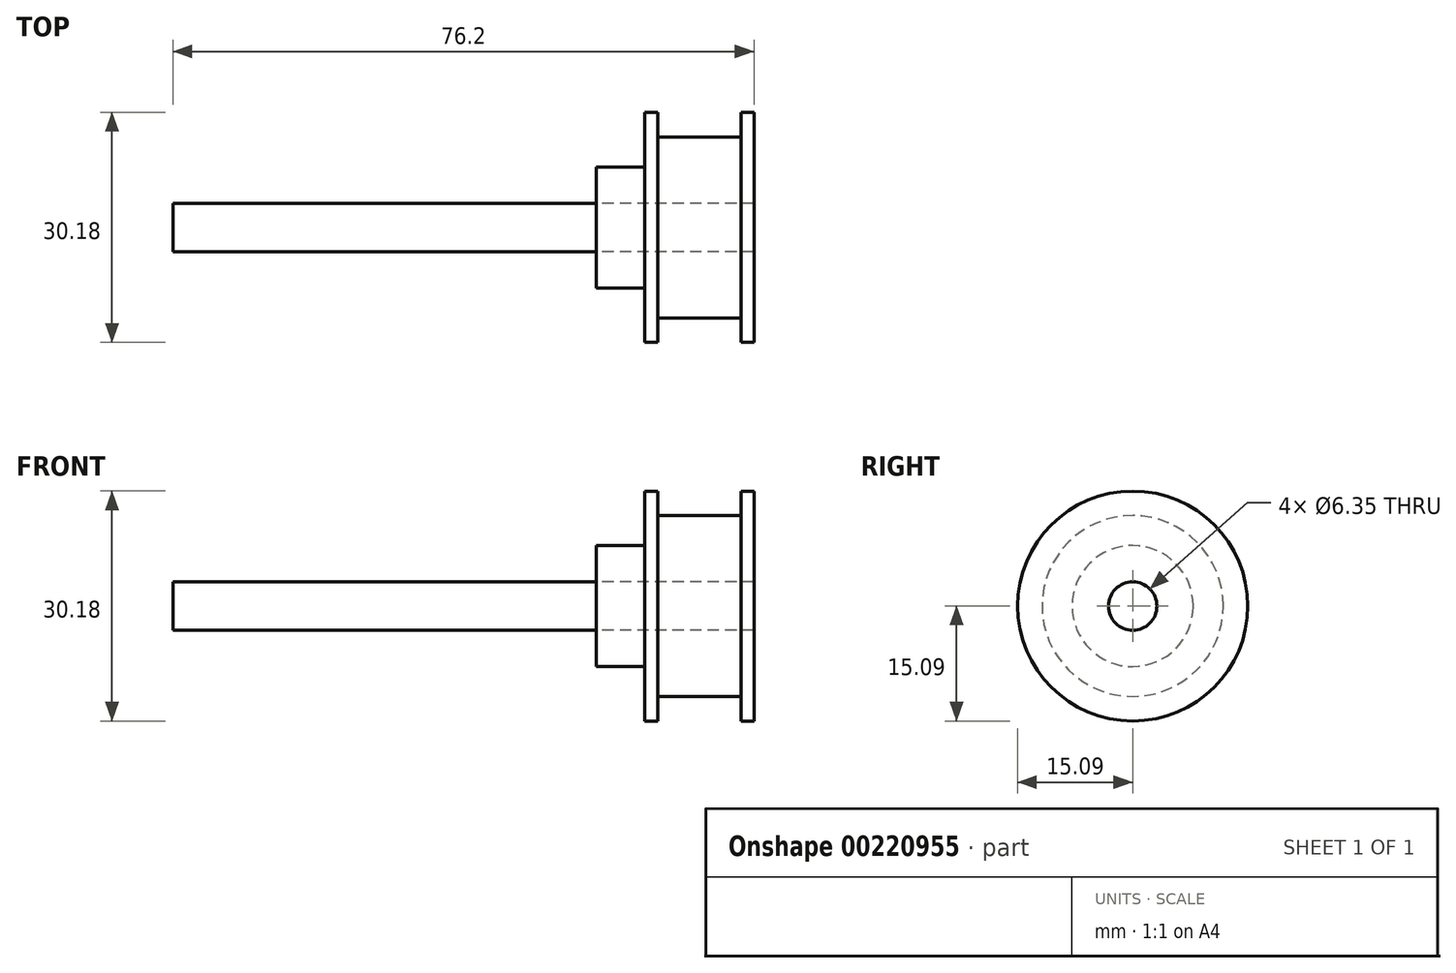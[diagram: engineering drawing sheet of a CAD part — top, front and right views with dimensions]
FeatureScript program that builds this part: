
annotation { "Feature Type Name" : "Feature", "Feature Type Description" : "" }
export const myFeature = defineFeature(function(context is Context, id is Id, definition is map)
    precondition{}
    {
        {
            var Q0;
            Q0=qCreatedBy(makeId("Front.planeOp"),FACE);
            var sketch = newSketch(context, id + "F0", { "sketchPlane" : qUnion([Q0])});
            skLineSegment(sketch, "E0", {"start": v(0, 3.18) * mm, "end": v(20.7, 3.18) * mm});
            skLineSegment(sketch, "E1", {"start": v(20.7, 3.18) * mm, "end": v(20.7, 15.09) * mm});
            skLineSegment(sketch, "E2", {"start": v(20.7, 15.09) * mm, "end": v(18.97, 15.09) * mm});
            skLineSegment(sketch, "E3", {"start": v(18.97, 15.09) * mm, "end": v(18.97, 11.87) * mm});
            skLineSegment(sketch, "E4", {"start": v(18.97, 11.87) * mm, "end": v(8.08, 11.87) * mm});
            skLineSegment(sketch, "E5", {"start": v(8.08, 11.87) * mm, "end": v(8.08, 15.09) * mm});
            skLineSegment(sketch, "E6", {"start": v(8.08, 15.09) * mm, "end": v(6.35, 15.09) * mm});
            skLineSegment(sketch, "E7", {"start": v(6.35, 15.09) * mm, "end": v(6.35, 7.94) * mm});
            skLineSegment(sketch, "E8", {"start": v(6.35, 7.94) * mm, "end": v(0, 7.94) * mm});
            skLineSegment(sketch, "E9", {"start": v(0, 7.94) * mm, "end": v(0, 3.18) * mm});
            skLineSegment(sketch, "E10", {"start": v(0, 0) * mm, "end": v(52.14, 0) * mm, "construction": true});
            skSolve(sketch);
        }
        {
            var Q0;
            Q0=makeQuery(id+"F0.imprint","IMPRINT",FACE,{"disambiguationData":[TD([[makeQuery(id+"F0.imprint","IMPRINT",EDGE,{"derivedFrom":sQuery(id+"F0.wireOp",EDGE,"E0")}),1.0]])]});
            var Q1;
            Q1=sQuery(id+"F0.wireOp",EDGE,"E10");
            revolve(context, id + "F1", {"entities" : qUnion([Q0]), "axis" : qUnion([Q1]), "revolveType" : RevolveType.FULL});
        }
        {
            var Q0;
            Q0=makeQuery(id+"F1.opRevolve","SWEPT_FACE",FACE,{"disambiguationData":[OSD([sQuery(id+"F0.wireOp",EDGE,"E1")])]});
            var sketch = newSketch(context, id + "F2", { "sketchPlane" : qUnion([Q0])});
            skCircle(sketch, "E11.0", {"center": v(0, 0) * mm, "radius": 3.18 * mm});
            skSolve(sketch);
        }
        {
            var Q0;
            Q0 = qSketchRegion(id + "F2", true);
            extrude(context, id + "F3", {"entities" : qUnion([Q0]), "oppositeDirection" : true, "depth" : 76.2 * mm});
        }
    });
